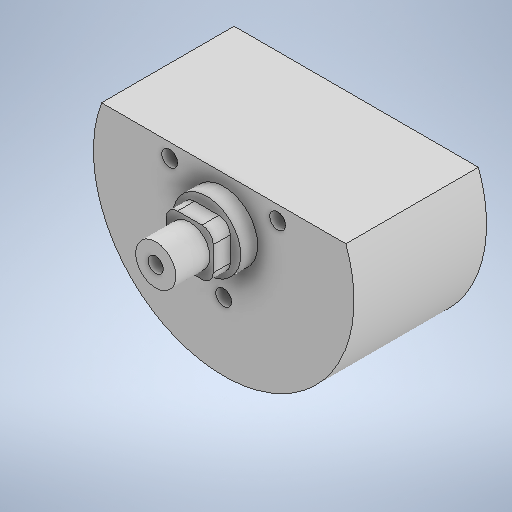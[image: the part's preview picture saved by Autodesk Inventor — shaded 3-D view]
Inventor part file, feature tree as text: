
AUTODESK INVENTOR PART (.ipt)
format: ipt  version: 2025.1 (Build 291241000, 241)  size: 262,656 bytes
history: native  units: mm
features: sketch x7, extrude x6, fillet x1, projected_geometry x1
ambient origin geometry x8: Origin, YZ Plane, XZ Plane, XY Plane, X Axis, Y Axis, Z Axis, Center Point
bodies: Solid1 (feature_tree)
feature tree (15):
  extrude  "Extrusion1"  Depth=8.0mm
  extrude  "Extrusion2"  Depth=12.0mm
  extrude  "Extrusion3"  Depth=8.3mm
  fillet  "Fillet1"  Radius=8.3mm
  extrude  "Extrusion4"  Depth=2.0mm
  extrude  "Extrusion5"  Depth=6.0mm TaperAngle=0.0deg
  extrude  "Extrusion6"  Depth=10.0mm TaperAngle=0.0deg
  sketch  "Sketch1"  dims[d0=46.0mm d1=8.0mm]
  sketch  "Sketch2"  dims[d5=3.0mm d6=0.0mm d7=8.3mm d8=8.3mm]
  sketch  "Sketch3"  dims[d9=3.0mm d10=0.0mm d11=2.0mm]
  sketch  "Sketch4"  dims[d12=7.1mm d13=6.0mm d14=0.0mm]
  sketch  "Sketch5"  dims[d15=2.7mm d16=10.0mm d17=0.0mm]
  sketch  "Sketch6"  dims[d18=2.8mm d19=11.0mm d20=30.0mm d22=360.0deg d24=10.0mm d25=0.0mm]
  projected_geometry  "Projected Loop1"
  sketch  "Sketch Circular Pattern1"  dims[d2=23.4mm d3=0.0mm d4=12.0mm]
